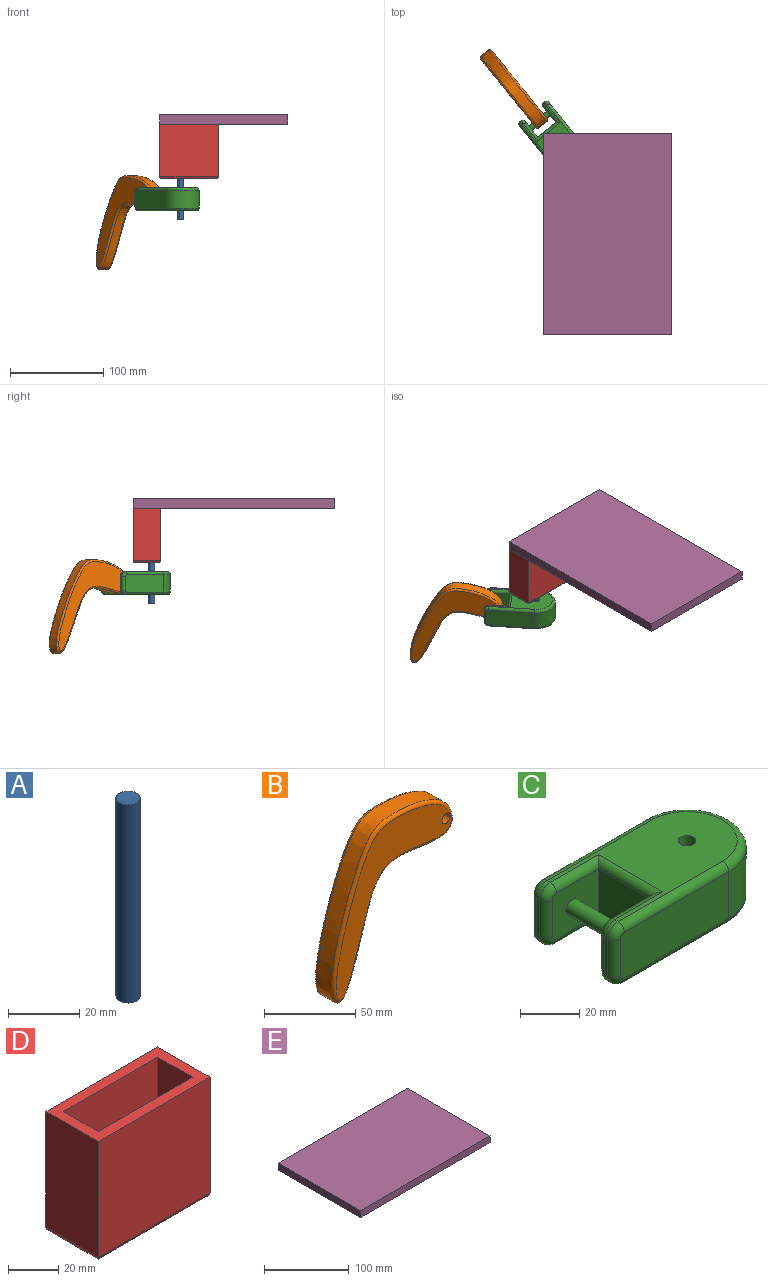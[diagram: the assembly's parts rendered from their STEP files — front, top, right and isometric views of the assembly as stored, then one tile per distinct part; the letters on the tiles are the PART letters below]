
ASSEMBLY  parts=5 mates=3
PART A: 3 faces, bbox 6.8x6.8x68.2 mm
  f0: cylinder r=3.39mm len=68.2mm, axis (0,0,1), area 1452.1mm2, adj f1,f2
  f1: plane 6.78x6.78mm, normal (0,0,-1), area 36.1mm2, adj f0
  f2: plane 6.78x6.78mm, normal (0,0,1), area 36.1mm2, adj f0
PART B: 6 faces, bbox 93x15x104.9 mm
  f0: extruded ~104.34x92.79mm, area 3563.1mm2, adj f4,f5
  f1: cylinder r=3.25mm len=15mm, axis (0,1,0), area 306.3mm2, adj f2,f3
  f2: plane 100.92x89.01mm, normal (0,-1,0), area 2591.9mm2, adj f1,f5
  f3: plane 100.91x89.01mm, normal (0,1,0), area 2584.1mm2, adj f1,f4
  f4: bspline ~104.91x93.01mm, area 995.1mm2, adj f0,f3
  f5: bspline ~104.92x93.01mm, area 1006.9mm2, adj f0,f2
PART C: 40 faces, bbox 76.6x43.3x25 mm
  f0: plane 52x19mm, normal (0,-1,0), area 986.3mm2, adj f7,f16,f18,f19,f31,f37
  f1: plane 22x19mm, normal (0,1,0), area 388mm2, adj f5,f11,f20,f21,f22,f33,f39
  f2: plane 22x19mm, normal (0,-1,0), area 388mm2, adj f5,f11,f25,f26,f27,f28,f34
  f3: plane 52x19mm, normal (0,1,0), area 986.3mm2, adj f7,f12,f13,f15,f30,f36
  f4: plane 15x1.5mm, normal (-1,0,0), area 22.5mm2, adj f13,f27,f29,f35
  f5: plane 25x19mm, normal (-1,0,0), area 475mm2, adj f1,f2,f23,f24
  f6: plane 15x1.5mm, normal (-1,0,0), area 22.5mm2, adj f18,f20,f32,f38
  f7: cylinder r=20mm len=40mm, axis (0,0,-1), area 1193.8mm2, adj f0,f3,f14,f17
  f8: cylinder r=3mm len=25mm, axis (0,0,-1), area 471.2mm2, adj f9,f10
  f9: plane 67x34mm, normal (0,0,1), area 1412.7mm2, adj f8,f15,f17,f19,f21,f23,f25,f29
  f10: plane 67x34mm, normal (0,0,-1), area 1412.7mm2, adj f8,f12,f14,f16,f22,f24,f26,f35
  f11: cylinder r=3mm len=25mm, axis (0,-1,0), area 471.2mm2, adj f1,f2
  f12: cylinder r=3mm len=50mm, axis (-1,0,0), area 235.6mm2, adj f3,f10,f14,f36
  f13: cylinder r=3mm len=15mm, axis (0,0,1), area 70.7mm2, adj f3,f4,f30,f36
  f14: torus R=17mm, axis (0,0,1), area 279.9mm2, adj f7,f10,f12,f16
  f15: cylinder r=3mm len=50mm, axis (1,0,0), area 235.6mm2, adj f3,f9,f17,f30
  f16: cylinder r=3mm len=50mm, axis (1,0,0), area 235.6mm2, adj f0,f10,f14,f37
  f17: torus R=17mm, axis (0,0,1), area 279.9mm2, adj f7,f9,f15,f19
  f18: cylinder r=3mm len=15mm, axis (0,0,-1), area 70.7mm2, adj f0,f6,f31,f37
  f19: cylinder r=3mm len=50mm, axis (-1,0,0), area 235.6mm2, adj f0,f9,f17,f31
  f20: cylinder r=3mm len=15mm, axis (0,0,1), area 70.7mm2, adj f1,f6,f33,f39
  f21: cylinder r=3mm len=23mm, axis (1,0,0), area 99.4mm2, adj f1,f9,f23,f33
  f22: cylinder r=3mm len=23mm, axis (-1,0,0), area 99.4mm2, adj f1,f10,f24,f39
  f23: cylinder r=3mm len=31mm, axis (0,1,0), area 128.1mm2, adj f5,f9,f21,f25
  f24: cylinder r=3mm len=31mm, axis (0,-1,0), area 128.1mm2, adj f5,f10,f22,f26
  f25: cylinder r=3mm len=23mm, axis (-1,0,0), area 99.4mm2, adj f2,f9,f23,f28
  f26: cylinder r=3mm len=23mm, axis (1,0,0), area 99.4mm2, adj f2,f10,f24,f34
  f27: cylinder r=3mm len=15mm, axis (0,0,-1), area 70.7mm2, adj f2,f4,f28,f34
  f28: torus R=2mm, axis (0,-1,0), area 28.9mm2, adj f2,f25,f27,f29
  f29: cylinder r=5mm len=5mm, axis (0,1,0), area 11.8mm2, adj f4,f9,f28,f30
  f30: torus R=2mm, axis (0,-1,0), area 28.9mm2, adj f3,f13,f15,f29
  f31: torus R=2mm, axis (0,-1,0), area 28.9mm2, adj f0,f18,f19,f32
  f32: cylinder r=5mm len=5mm, axis (0,1,0), area 11.8mm2, adj f6,f9,f31,f33
  f33: torus R=2mm, axis (0,-1,0), area 28.9mm2, adj f1,f20,f21,f32
  f34: torus R=2mm, axis (0,-1,0), area 28.9mm2, adj f2,f26,f27,f35
  f35: cylinder r=5mm len=5mm, axis (0,-1,0), area 11.8mm2, adj f4,f10,f34,f36
  f36: torus R=2mm, axis (0,-1,0), area 28.9mm2, adj f3,f12,f13,f35
  f37: torus R=2mm, axis (0,-1,0), area 28.9mm2, adj f0,f16,f18,f38
  f38: cylinder r=5mm len=5mm, axis (0,-1,0), area 11.8mm2, adj f6,f10,f37,f39
  f39: torus R=2mm, axis (0,-1,0), area 28.9mm2, adj f1,f20,f22,f38
PART D: 26 faces, bbox 63x29.4x58.4 mm
  f0: plane 19.4x6.5mm, normal (-1,0,0), area 126.1mm2, adj f3,f9,f16,f21
  f1: plane 19.4x6.5mm, normal (1,0,0), area 126.1mm2, adj f3,f9,f13,f18
  f2: plane 44.9x19.4mm, normal (1,0,0), area 871.1mm2, adj f3,f9,f10,f14
  f3: plane 56.4x53mm, normal (0,-1,0), area 2926.2mm2, adj f0,f1,f2,f4,f10,f12,f13,f14
  f4: plane 44.9x19.4mm, normal (-1,0,0), area 871.1mm2, adj f3,f9,f10,f17
  f5: plane 56.4x29.4mm, normal (-1,0,0), area 1658.2mm2, adj f6,f8,f10,f23
  f6: plane 63x56.4mm, normal (0,-1,0), area 3553.2mm2, adj f5,f7,f10,f22
  f7: plane 56.4x29.4mm, normal (1,0,0), area 1658.2mm2, adj f6,f8,f10,f24
  f8: plane 63x56.4mm, normal (0,1,0), area 3553.2mm2, adj f5,f7,f10,f25
  f9: plane 56.4x53mm, normal (0,1,0), area 2926.2mm2, adj f0,f1,f2,f4,f10,f12,f13,f14
  f10: plane 63x29.4mm, normal (0,0,1), area 824mm2, adj f2,f3,f4,f5,f6,f7,f8,f9
  f11: plane 59x25.4mm, normal (0,0,-1), area 164.8mm2, adj f18,f19,f20,f21,f22,f23,f24,f25
  f12: plane 19.4x5mm, normal (1,0,0), area 97mm2, adj f3,f9,f13,f14
  f13: plane 19.4x6.3mm, normal (0,0,-1), area 122.2mm2, adj f1,f3,f9,f12
  f14: plane 19.4x6.3mm, normal (0,0,1), area 122.2mm2, adj f2,f3,f9,f12
  f15: plane 19.4x5mm, normal (-1,0,0), area 97mm2, adj f3,f9,f16,f17
  f16: plane 19.4x6.3mm, normal (0,0,-1), area 122.2mm2, adj f0,f3,f9,f15
  f17: plane 19.4x6.3mm, normal (0,0,1), area 122.2mm2, adj f3,f4,f9,f15
  f18: cylinder r=2mm len=23.4mm, axis (0,1,0), area 65.5mm2, adj f1,f11,f19,f20
  f19: cylinder r=2mm len=57mm, axis (1,0,0), area 171.1mm2, adj f3,f11,f18,f21
  f20: cylinder r=2mm len=57mm, axis (-1,0,0), area 171.1mm2, adj f9,f11,f18,f21
  f21: cylinder r=2mm len=23.4mm, axis (0,-1,0), area 65.5mm2, adj f0,f11,f19,f20
  f22: cylinder r=2mm len=63mm, axis (1,0,0), area 193.4mm2, adj f6,f11,f23,f24
  f23: cylinder r=2mm len=29.4mm, axis (0,-1,0), area 87.8mm2, adj f5,f11,f22,f25
  f24: cylinder r=2mm len=29.4mm, axis (0,1,0), area 87.8mm2, adj f7,f11,f22,f25
  f25: cylinder r=2mm len=63mm, axis (-1,0,0), area 193.4mm2, adj f8,f11,f23,f24
PART E: 6 faces, bbox 216.4x137.6x10 mm
  f0: plane 137.59x10mm, normal (-1,0,0), area 1375.9mm2, adj f1,f3,f4,f5
  f1: plane 216.44x10mm, normal (0,-1,0), area 2164.4mm2, adj f0,f2,f4,f5
  f2: plane 137.59x10mm, normal (1,0,0), area 1375.9mm2, adj f1,f3,f4,f5
  f3: plane 216.44x10mm, normal (0,1,0), area 2164.4mm2, adj f0,f2,f4,f5
  f4: plane 216.44x137.59mm, normal (0,0,1), area 29780.4mm2, adj f0,f1,f2,f3
  f5: plane 216.44x137.59mm, normal (0,0,-1), area 29780.4mm2, adj f0,f1,f2,f3
PLACE A t=(-78.12,-161.33,64.6)mm fixed
PLACE B rot(axis=(0.05,0.1,-0.99),51.3deg) t=(-118.83,-128.27,18)mm
PLACE C rot(axis=(0,0,-1),51.1deg) t=(-83.57,-171.91,18)mm
PLACE D t=(-82.79,-156.39,69.52)mm fixed
PLACE E rot(axis=(0,0,-1),90deg) t=(-45.49,-249.91,103.72)mm
MATE revolute C.f7 <-> A.f0  axis (0,0,1) through (-92.12,-161.33,30.5)mm
MATE fastened E.f5 <-> D.f10  axis (0,0,1) through (-114.29,-141.69,98.72)mm
MATE revolute B.f1 <-> C.f11  axis (0.78,0.63,0) through (-113,-123.56,18)mm
